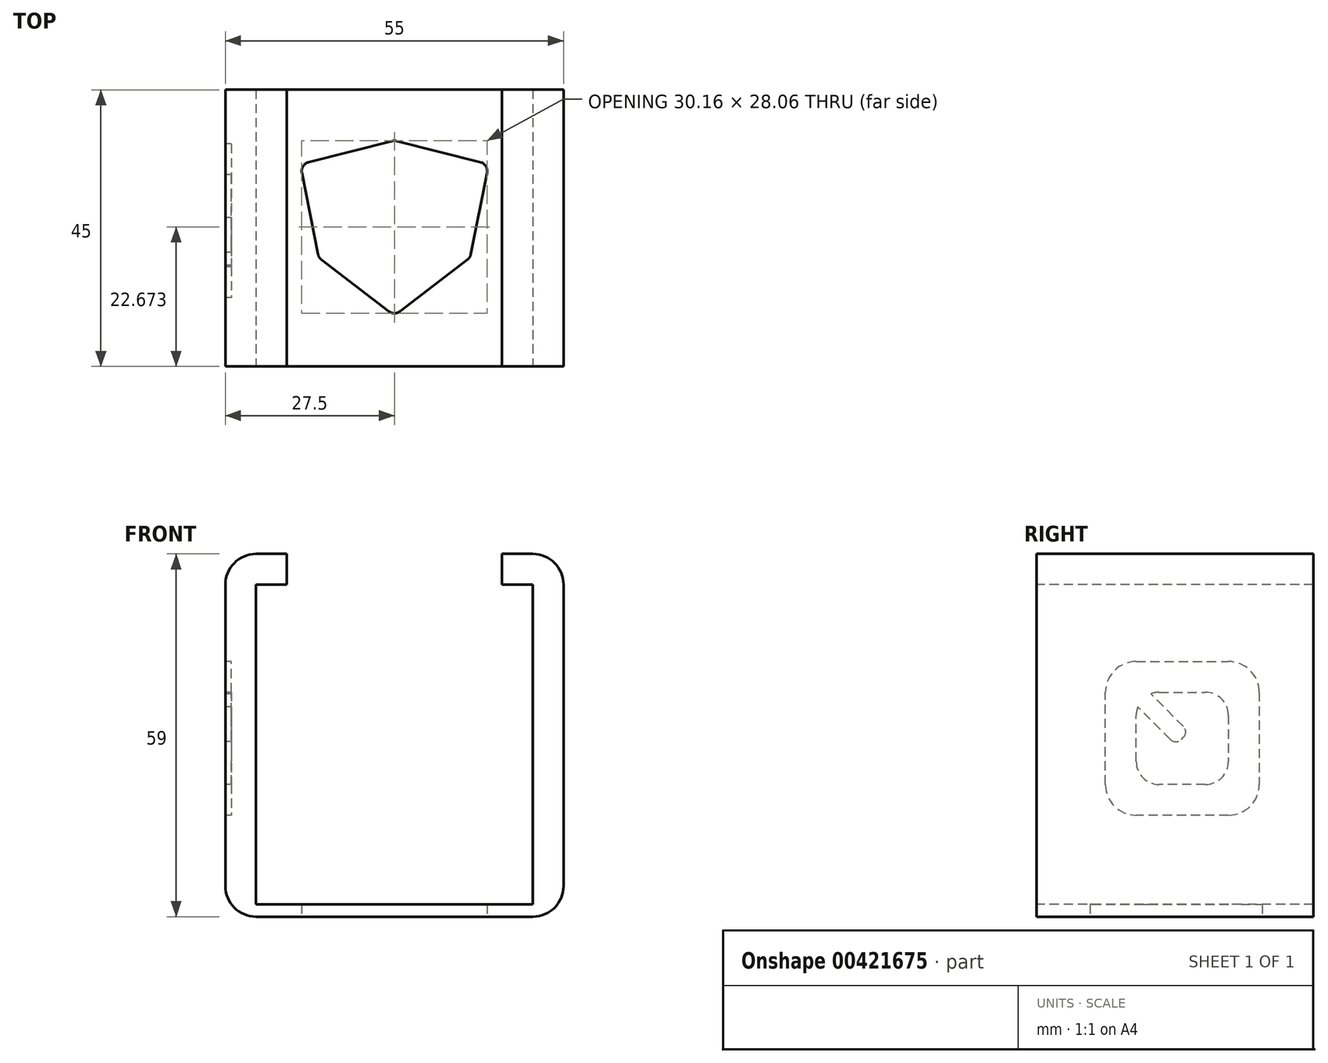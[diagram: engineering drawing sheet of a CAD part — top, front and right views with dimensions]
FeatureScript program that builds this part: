
annotation { "Feature Type Name" : "Feature", "Feature Type Description" : "" }
export const myFeature = defineFeature(function(context is Context, id is Id, definition is map)
    precondition{}
    {
        {
            var Q0;
            Q0=qCreatedBy(makeId("Top.planeOp"),FACE);
            var sketch = newSketch(context, id + "F0", { "sketchPlane" : qUnion([Q0])});
            skLineSegment(sketch, "E0", {"start": v(-13.95, 15.55) * mm, "end": v(-0.37, 18.98) * mm});
            skLineSegment(sketch, "E1", {"start": v(0.37, 18.98) * mm, "end": v(13.95, 15.55) * mm});
            skLineSegment(sketch, "E2", {"start": v(-15.05, 13.8) * mm, "end": v(-12.41, 0.55) * mm});
            skLineSegment(sketch, "E3", {"start": v(-11.85, -0.34) * mm, "end": v(-0.91, -8.73) * mm});
            skLineSegment(sketch, "E4", {"start": v(0.91, -8.73) * mm, "end": v(11.85, -0.34) * mm});
            skLineSegment(sketch, "E5", {"start": v(12.41, 0.55) * mm, "end": v(15.05, 13.8) * mm});
            skPoint(sketch, "E6.visualSharp", {"position": v(0, 19.07) * mm});
            skArc(sketch, "E6.filletArc", {"start": v(0.37, 18.98) * mm, "mid": v(0, 19.02) * mm, "end": v(-0.37, 18.98) * mm});
            skPoint(sketch, "E7.visualSharp", {"position": v(-15.33, 15.2) * mm});
            skArc(sketch, "E7.filletArc", {"start": v(-13.95, 15.55) * mm, "mid": v(-14.85, 14.9) * mm, "end": v(-15.05, 13.8) * mm});
            skPoint(sketch, "E8.visualSharp", {"position": v(0, -9.43) * mm});
            skArc(sketch, "E8.filletArc", {"start": v(-0.91, -8.73) * mm, "mid": v(0, -9.04) * mm, "end": v(0.91, -8.73) * mm});
            skPoint(sketch, "E9.visualSharp", {"position": v(15.33, 15.2) * mm});
            skArc(sketch, "E9.filletArc", {"start": v(15.05, 13.8) * mm, "mid": v(14.85, 14.9) * mm, "end": v(13.95, 15.55) * mm});
            skPoint(sketch, "E10.visualSharp", {"position": v(-12.3, 0) * mm});
            skArc(sketch, "E10.filletArc", {"start": v(-12.41, 0.55) * mm, "mid": v(-12.22, 0.05) * mm, "end": v(-11.85, -0.34) * mm});
            skPoint(sketch, "E11.visualSharp", {"position": v(12.3, 0) * mm});
            skArc(sketch, "E11.filletArc", {"start": v(11.85, -0.34) * mm, "mid": v(12.22, 0.05) * mm, "end": v(12.41, 0.55) * mm});
            skLineSegment(sketch, "E12.bottom", {"start": v(-22.5, 27.32) * mm, "end": v(22.5, 27.32) * mm});
            skLineSegment(sketch, "E12.top", {"start": v(-22.5, -17.68) * mm, "end": v(22.5, -17.68) * mm});
            skLineSegment(sketch, "E12.left", {"start": v(-22.5, 27.32) * mm, "end": v(-22.5, -17.68) * mm});
            skLineSegment(sketch, "E12.right", {"start": v(22.5, 27.32) * mm, "end": v(22.5, -17.68) * mm});
            skLineSegment(sketch, "E13", {"start": v(15.33, 15.2) * mm, "end": v(22.5, 15.2) * mm, "construction": true});
            skLineSegment(sketch, "E14", {"start": v(-15.33, 15.2) * mm, "end": v(-22.5, 15.2) * mm, "construction": true});
            skLineSegment(sketch, "E15", {"start": v(0, 19.07) * mm, "end": v(0, 27.32) * mm, "construction": true});
            skLineSegment(sketch, "E16", {"start": v(0, -9.43) * mm, "end": v(0, -17.68) * mm, "construction": true});
            skLineSegment(sketch, "E17.bottom", {"start": v(-16.5, 23.07) * mm, "end": v(16.5, 23.07) * mm, "construction": true});
            skLineSegment(sketch, "E17.top", {"start": v(-16.5, -13.43) * mm, "end": v(16.5, -13.43) * mm, "construction": true});
            skLineSegment(sketch, "E17.left", {"start": v(-16.5, 23.07) * mm, "end": v(-16.5, -13.43) * mm, "construction": true});
            skLineSegment(sketch, "E17.right", {"start": v(16.5, 23.07) * mm, "end": v(16.5, -13.43) * mm, "construction": true});
            skLineSegment(sketch, "E18", {"start": v(0, -9.43) * mm, "end": v(-16.5, -9.43) * mm, "construction": true});
            skLineSegment(sketch, "E19", {"start": v(0, -9.43) * mm, "end": v(16.5, -9.43) * mm, "construction": true});
            skLineSegment(sketch, "E20", {"start": v(-13.58, 14.1) * mm, "end": v(13.58, 14.1) * mm, "construction": true});
            skLineSegment(sketch, "E21", {"start": v(-10.94, 0.85) * mm, "end": v(10.94, 0.85) * mm, "construction": true});
            skSolve(sketch);
        }
        {
            var Q0;
            Q0=makeQuery(id+"F0.imprint","IMPRINT",FACE,{"disambiguationData":[TD([[makeQuery(id+"F0.imprint","IMPRINT",EDGE,{"derivedFrom":sQuery(id+"F0.wireOp",EDGE,"E0")}),1.0]])]});
            extrude(context, id + "F1", {"entities" : qUnion([Q0]), "depth" : 2 * mm});
        }
        {
            var Q0;
            Q0=makeQuery(id+"F1.opExtrude","SWEPT_FACE",FACE,{"disambiguationData":[OSD([sQuery(id+"F0.wireOp",EDGE,"E12.left")])]});
            extrude(context, id + "F2", {"entities" : qUnion([Q0]), "operationType" : NewBodyOperationType.ADD, "depth" : 5 * mm});
        }
        {
            var Q0;
            Q0=makeQuery(id+"F1.opExtrude","SWEPT_FACE",FACE,{"disambiguationData":[OSD([sQuery(id+"F0.wireOp",EDGE,"E12.right")])]});
            extrude(context, id + "F3", {"entities" : qUnion([Q0]), "operationType" : NewBodyOperationType.ADD, "depth" : 5 * mm});
        }
        {
            var Q0;
            {var subQ0=sQuery(id+"F0.wireOp",EDGE,"E12.right");var subQ1=sQuery(id+"F0.wireOp",EDGE,"E12.left");Q0=makeQuery(id+"F3.boolean.opBoolean","MERGE",FACE,{"derivedFrom":[makeQuery(id+"F2.boolean.opBoolean","MERGE",FACE,{"derivedFrom":[makeQuery(id+"F1.opExtrude","CAP_FACE",FACE,{"disambiguationData":[OSD([sQuery(id+"F0.wireOp",EDGE,"E0"),sQuery(id+"F0.wireOp",EDGE,"E1"),sQuery(id+"F0.wireOp",EDGE,"E2"),sQuery(id+"F0.wireOp",EDGE,"E3"),sQuery(id+"F0.wireOp",EDGE,"E4"),sQuery(id+"F0.wireOp",EDGE,"E5"),sQuery(id+"F0.wireOp",EDGE,"E6.filletArc"),sQuery(id+"F0.wireOp",EDGE,"E7.filletArc"),sQuery(id+"F0.wireOp",EDGE,"E8.filletArc"),sQuery(id+"F0.wireOp",EDGE,"E9.filletArc"),sQuery(id+"F0.wireOp",EDGE,"E10.filletArc"),sQuery(id+"F0.wireOp",EDGE,"E11.filletArc"),sQuery(id+"F0.wireOp",EDGE,"E12.bottom"),sQuery(id+"F0.wireOp",EDGE,"E12.top"),subQ1,subQ0])],"isStart":false}),makeQuery(id+"F2.opExtrude","SWEPT_FACE",FACE,{"disambiguationData":[OSD([subQ1]),TDD([makeQuery(id+"F1.opExtrude","CAP_EDGE",EDGE,{"disambiguationData":[OSD([subQ1])],"isStart":false})])]})]}),makeQuery(id+"F3.opExtrude","SWEPT_FACE",FACE,{"disambiguationData":[OSD([subQ0]),TDD([makeQuery(id+"F1.opExtrude","CAP_EDGE",EDGE,{"disambiguationData":[OSD([subQ0])],"isStart":false})])]})]});}
            var sketch = newSketch(context, id + "F4", { "sketchPlane" : qUnion([Q0])});
            skLineSegment(sketch, "E22", {"start": v(-22.5, 27.32) * mm, "end": v(-22.5, -17.68) * mm});
            skLineSegment(sketch, "E23", {"start": v(22.5, 27.32) * mm, "end": v(22.5, -17.68) * mm});
            skSolve(sketch);
        }
        {
            var Q0;
            {var subQ0=sQuery(id+"F4.wireOp",EDGE,"E22");Q0=makeQuery(id+"F4.imprint","IMPRINT",FACE,{"disambiguationData":[TD([[makeQuery(id+"F4.imprint","IMPRINT",EDGE,{"derivedFrom":subQ0}),-1.0]])]});}
            var Q1;
            {var subQ0=sQuery(id+"F4.wireOp",EDGE,"E23");Q1=makeQuery(id+"F4.imprint","IMPRINT",FACE,{"disambiguationData":[TD([[makeQuery(id+"F4.imprint","IMPRINT",EDGE,{"derivedFrom":subQ0}),1.0]])]});}
            extrude(context, id + "F5", {"entities" : qUnion([Q0, Q1]), "operationType" : NewBodyOperationType.ADD, "depth" : 57 * mm});
        }
        {
            var Q0;
            Q0=makeQuery(id+"F5.opExtrude","SWEPT_FACE",FACE,{"disambiguationData":[OSD([sQuery(id+"F4.wireOp",EDGE,"E22")])]});
            var sketch = newSketch(context, id + "F6", { "sketchPlane" : qUnion([Q0])});
            skLineSegment(sketch, "E24", {"start": v(-17.68, 54) * mm, "end": v(27.32, 54) * mm});
            skSolve(sketch);
        }
        {
            var Q0;
            Q0=makeQuery(id+"F5.opExtrude","SWEPT_FACE",FACE,{"disambiguationData":[OSD([sQuery(id+"F4.wireOp",EDGE,"E23")])]});
            var sketch = newSketch(context, id + "F7", { "sketchPlane" : qUnion([Q0])});
            skLineSegment(sketch, "E25", {"start": v(-27.32, 54) * mm, "end": v(17.68, 54) * mm});
            skSolve(sketch);
        }
        {
            var Q0;
            {var subQ0=sQuery(id+"F7.wireOp",EDGE,"E25");Q0=makeQuery(id+"F7.imprint","IMPRINT",FACE,{"disambiguationData":[TD([[makeQuery(id+"F7.imprint","IMPRINT",EDGE,{"derivedFrom":subQ0}),1.0]])]});}
            extrude(context, id + "F8", {"entities" : qUnion([Q0]), "operationType" : NewBodyOperationType.ADD, "depth" : 5 * mm});
        }
        {
            var Q0;
            {var subQ0=sQuery(id+"F6.wireOp",EDGE,"E24");Q0=makeQuery(id+"F6.imprint","IMPRINT",FACE,{"disambiguationData":[TD([[makeQuery(id+"F6.imprint","IMPRINT",EDGE,{"derivedFrom":subQ0}),1.0]])]});}
            extrude(context, id + "F9", {"entities" : qUnion([Q0]), "operationType" : NewBodyOperationType.ADD, "depth" : 5 * mm});
        }
        {
            var Q0;
            {var subQ0=sQuery(id+"F0.wireOp",EDGE,"E12.right");Q0=makeQuery(id+"F3.opExtrude","CAP_EDGE",EDGE,{"disambiguationData":[OSD([subQ0]),TDD([makeQuery(id+"F1.opExtrude","CAP_EDGE",EDGE,{"disambiguationData":[OSD([subQ0])],"isStart":true})])],"isStart":false});}
            var Q1;
            {var subQ0=sQuery(id+"F0.wireOp",EDGE,"E12.left");Q1=makeQuery(id+"F2.opExtrude","CAP_EDGE",EDGE,{"disambiguationData":[OSD([subQ0]),TDD([makeQuery(id+"F1.opExtrude","CAP_EDGE",EDGE,{"disambiguationData":[OSD([subQ0])],"isStart":true})])],"isStart":false});}
            var Q2;
            Q2=makeQuery(id+"F5.opExtrude","CAP_EDGE",EDGE,{"disambiguationData":[OSD([sQuery(id+"F0.wireOp",EDGE,"E12.left")])],"isStart":false});
            var Q3;
            Q3=makeQuery(id+"F5.opExtrude","CAP_EDGE",EDGE,{"disambiguationData":[OSD([sQuery(id+"F0.wireOp",EDGE,"E12.right")])],"isStart":false});
            fillet(context, id + "F10", {"entities" : qUnion([Q0, Q1, Q2, Q3]), "radius" : 5 * mm, "tangentPropagation" : true, "allowEdgeOverflow" : false});
        }
        {
            var Q0;
            {var subQ0=sQuery(id+"F0.wireOp",EDGE,"E12.left");Q0=makeQuery(id+"F5.boolean.opBoolean","MERGE",FACE,{"derivedFrom":[makeQuery(id+"F2.opExtrude","CAP_FACE",FACE,{"disambiguationData":[OSD([subQ0])],"isStart":false}),makeQuery(id+"F5.opExtrude","SWEPT_FACE",FACE,{"disambiguationData":[OSD([subQ0])]})]});}
            var sketch = newSketch(context, id + "F11", { "sketchPlane" : qUnion([Q0])});
            skLineSegment(sketch, "E26", {"start": v(6.5, 21.5) * mm, "end": v(6.5, 36.5) * mm});
            skLineSegment(sketch, "E27", {"start": v(1.5, 41.5) * mm, "end": v(-13.5, 41.5) * mm});
            skLineSegment(sketch, "E28", {"start": v(-18.5, 36.5) * mm, "end": v(-18.5, 21.5) * mm});
            skLineSegment(sketch, "E29", {"start": v(-13.5, 16.5) * mm, "end": v(1.5, 16.5) * mm});
            skArc(sketch, "E30", {"start": v(-18.5, 21.5) * mm, "mid": v(-17.04, 17.96) * mm, "end": v(-13.5, 16.5) * mm});
            skArc(sketch, "E31", {"start": v(-13.5, 41.5) * mm, "mid": v(-17.04, 40.04) * mm, "end": v(-18.5, 36.5) * mm});
            skArc(sketch, "E32", {"start": v(1.5, 16.5) * mm, "mid": v(5.04, 17.96) * mm, "end": v(6.5, 21.5) * mm});
            skArc(sketch, "E33", {"start": v(6.5, 36.5) * mm, "mid": v(5.04, 40.04) * mm, "end": v(1.5, 41.5) * mm});
            skLineSegment(sketch, "E34", {"start": v(1.5, 25.25) * mm, "end": v(1.5, 32.75) * mm});
            skLineSegment(sketch, "E35", {"start": v(-2.25, 36.5) * mm, "end": v(-9.75, 36.5) * mm});
            skLineSegment(sketch, "E36", {"start": v(-13.5, 32.75) * mm, "end": v(-13.5, 25.25) * mm});
            skLineSegment(sketch, "E37", {"start": v(-9.75, 21.5) * mm, "end": v(-2.25, 21.5) * mm});
            skArc(sketch, "E38", {"start": v(-13.5, 25.25) * mm, "mid": v(-12.4, 22.6) * mm, "end": v(-9.75, 21.5) * mm});
            skArc(sketch, "E39", {"start": v(-9.75, 36.5) * mm, "mid": v(-12.4, 35.4) * mm, "end": v(-13.5, 32.75) * mm});
            skArc(sketch, "E40", {"start": v(-2.25, 21.5) * mm, "mid": v(0.4, 22.6) * mm, "end": v(1.5, 25.25) * mm});
            skLineSegment(sketch, "E41", {"start": v(-6, 29) * mm, "end": v(-6.18, 29.18) * mm});
            skLineSegment(sketch, "E42", {"start": v(-6.18, 30.94) * mm, "end": v(-0.88, 36.24) * mm});
            skLineSegment(sketch, "E43", {"start": v(-4.06, 28.82) * mm, "end": v(1.24, 34.12) * mm});
            skArc(sketch, "E44", {"start": v(-6.18, 30.94) * mm, "mid": v(-6.54, 30.06) * mm, "end": v(-6.18, 29.18) * mm});
            skArc(sketch, "E45", {"start": v(-5.82, 28.82) * mm, "mid": v(-4.94, 28.46) * mm, "end": v(-4.06, 28.82) * mm});
            skArc(sketch, "E46", {"start": v(1.5, 32.75) * mm, "mid": v(1.43, 33.45) * mm, "end": v(1.24, 34.12) * mm});
            skArc(sketch, "E47", {"start": v(-0.88, 36.24) * mm, "mid": v(-1.55, 36.43) * mm, "end": v(-2.25, 36.5) * mm});
            skLineSegment(sketch, "E48", {"start": v(-5.82, 28.82) * mm, "end": v(-6, 29) * mm});
            skSolve(sketch);
        }
        {
            var Q0;
            Q0=makeQuery(id+"F11.imprint","IMPRINT",FACE,{"disambiguationData":[TD([[makeQuery(id+"F11.imprint","IMPRINT",EDGE,{"derivedFrom":sQuery(id+"F11.wireOp",EDGE,"E26")}),1.0]])]});
            extrude(context, id + "F12", {"entities" : qUnion([Q0]), "operationType" : NewBodyOperationType.REMOVE, "oppositeDirection" : true, "depth" : 1 * mm});
        }
    });
